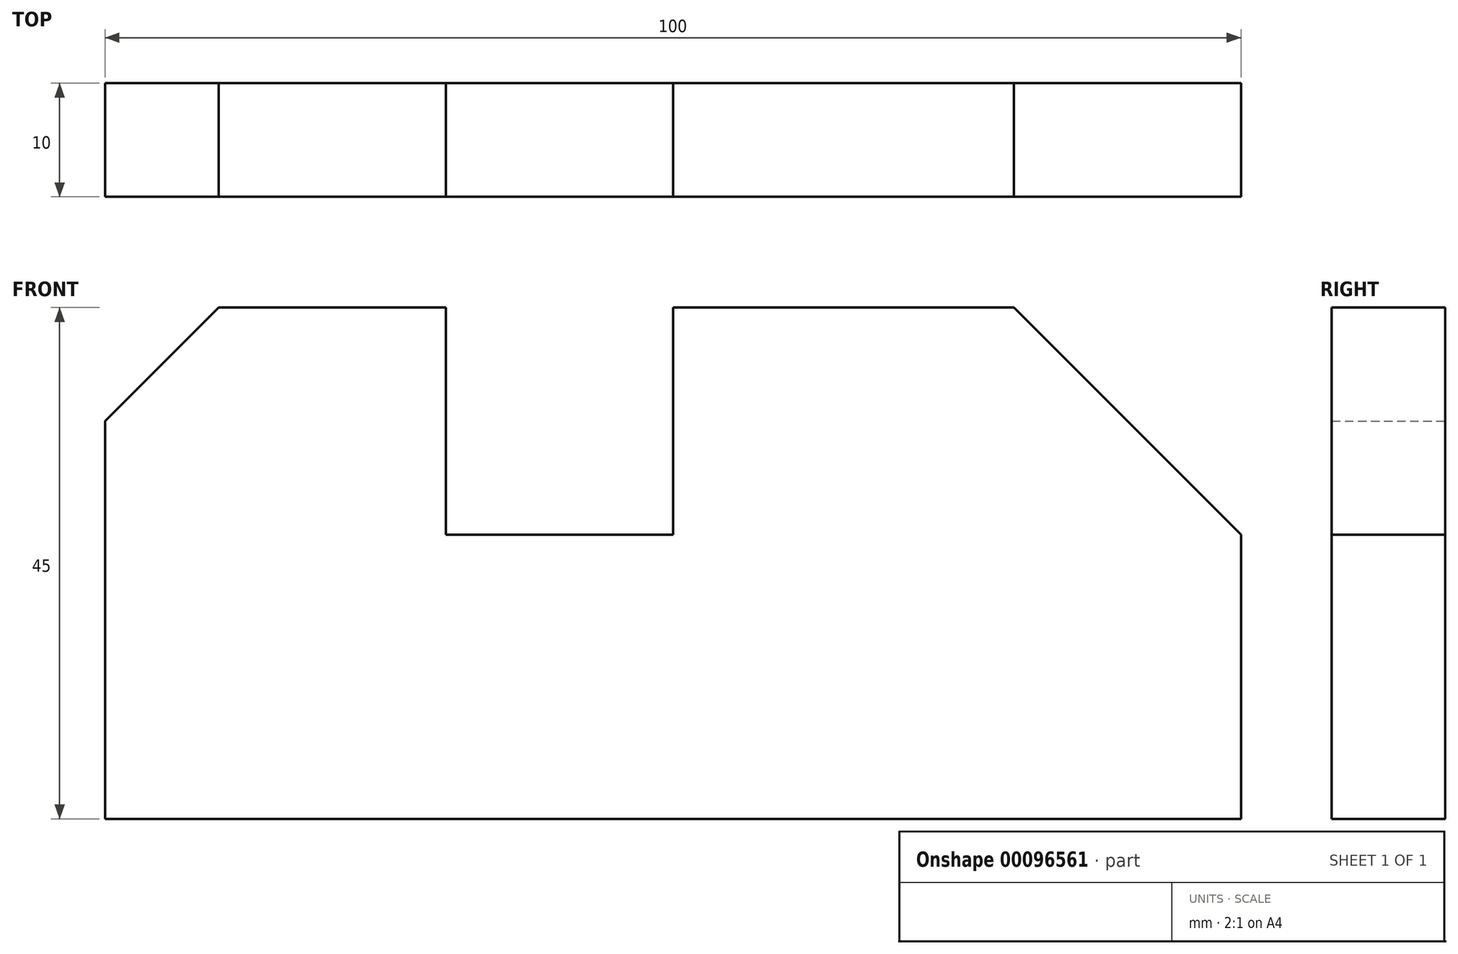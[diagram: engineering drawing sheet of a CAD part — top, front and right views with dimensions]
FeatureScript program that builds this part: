
annotation { "Feature Type Name" : "Feature", "Feature Type Description" : "" }
export const myFeature = defineFeature(function(context is Context, id is Id, definition is map)
    precondition{}
    {
        {
            var Q0;
            Q0=qCreatedBy(makeId("Front.planeOp"),FACE);
            var sketch = newSketch(context, id + "F0", { "sketchPlane" : qUnion([Q0])});
            skLineSegment(sketch, "E0", {"start": v(0, 0) * mm, "end": v(0, 35) * mm});
            skLineSegment(sketch, "E1", {"start": v(0, 35) * mm, "end": v(10, 45) * mm});
            skLineSegment(sketch, "E2", {"start": v(10, 45) * mm, "end": v(30, 45) * mm});
            skLineSegment(sketch, "E3", {"start": v(30, 45) * mm, "end": v(30, 25) * mm});
            skLineSegment(sketch, "E4", {"start": v(30, 25) * mm, "end": v(50, 25) * mm});
            skLineSegment(sketch, "E5", {"start": v(50, 25) * mm, "end": v(50, 45) * mm});
            skLineSegment(sketch, "E6", {"start": v(50, 45) * mm, "end": v(80, 45) * mm});
            skLineSegment(sketch, "E7", {"start": v(80, 45) * mm, "end": v(100, 25) * mm});
            skLineSegment(sketch, "E8", {"start": v(100, 25) * mm, "end": v(100, 0) * mm});
            skLineSegment(sketch, "E9", {"start": v(100, 0) * mm, "end": v(0, 0) * mm});
            skSolve(sketch);
        }
        {
            var Q0;
            Q0 = qSketchRegion(id + "F0", true);
            extrude(context, id + "F1", {"entities" : qUnion([Q0]), "depth" : 10 * mm});
        }
    });
